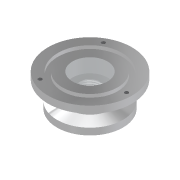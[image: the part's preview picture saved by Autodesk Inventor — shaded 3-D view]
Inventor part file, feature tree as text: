
AUTODESK INVENTOR PART (.ipt)
format: ipt  version: 2020 (Build 240168000, 168)  size: 363,008 bytes
history: native  units: in
note: dims shown in document units (in); Inventor stores cm internally (conversion verified against a paired STEP export)
features: sketch x4, revolve x2, hole x1, helix x1, other x1
ambient origin geometry x8: Origin, YZ Plane, XZ Plane, XY Plane, X Axis, Y Axis, Z Axis, Center Point
bodies: Solid1 (feature_tree)
feature tree (9):
  revolve  "Revolution1"  [1 undecoded]
  hole  "Hole1"  [1 undecoded]
  helix  "Coil1"  [1 undecoded]
  revolve  "Revolution2"  [1 undecoded]
  sketch  "Sketch1"  dims[d3=0.125in d4=0.75in]
  sketch  "Sketch4"  dims[d5=90.0deg d14=0.08in d15=0.4945in]
  sketch  "Sketch8"  dims[d16=0.06in d17=0.98in]
  sketch  "Sketch9"  dims[d18=0.067in d19=0.172in d20=0.375in d21=0.25in d22=0.5635in d23=0.261in d24=0.8108in d39=0.25in d40=0.3125in d43=0.12in d45=0.45in d47=0.59in d48=0.345in d50=15.0deg d51=0.383in d52=2.4531in d53=0.17in d55=0.0315in d56=60.0deg d57=0.0079in d58=0.1in d61=0.3267in d62=0.6533in d63=0.037in d64=1.0in d65=2.7559in d66=-0.0206in d67=90.0deg d68=90.0deg d69=0.0in d70=0.0in d71=45.0deg d72=0.0185in d73=45.0deg d74=90.0deg]
  other  "Dead Volume"
note: 4 required parameter values undecoded (feature->parameter linkage not recoverable at this tier; creation-order binding heuristic only, values carry confidence <= 0.55)